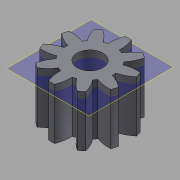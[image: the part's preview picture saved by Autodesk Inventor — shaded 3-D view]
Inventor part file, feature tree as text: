
AUTODESK INVENTOR PART (.ipt)
format: ipt  version: 2015 (Build 190159000, 159)  size: 184,320 bytes
history: native  units: mm (DEFAULTED — no unit token found)
features: plane x4, other x3, sketch x3, extrude x2
ambient origin geometry x8: Origin, YZ Plane, XZ Plane, XY Plane, X Axis, Y Axis, Z Axis, Center Point
bodies: Solid1 (feature_tree)
feature tree (12):
  extrude  "Extrusion1"  Depth=4.0mm TaperAngle=0.0deg
  plane  "Work Plane2"
  plane  "Work Plane8"
  plane  "Work Plane9"
  other  "Spur Gear"
  extrude  "Extrusion2"  Depth=10.0mm TaperAngle=0.0deg
  plane  "Work Plane12"
  sketch  "Sketch1"  dims[d0=6.0mm d1=4.0mm d2=0.0mm]
  sketch  "Sketch2"  dims[d3=5.0mm d4=10.0mm d5=0.0mm]
  other  "Srf1"
  sketch  "Sketch3"  dims[d16=11.5mm d17=0.0mm d34=3.141593mm d39=0.0mm d41=0.0mm d43=11.5mm d46=11.5mm d47=0.0mm d48=0.0mm d49=2.0mm d50=10.0mm d51=0.0mm d53=-3.5mm]
  other  "Pitch Diameter"
